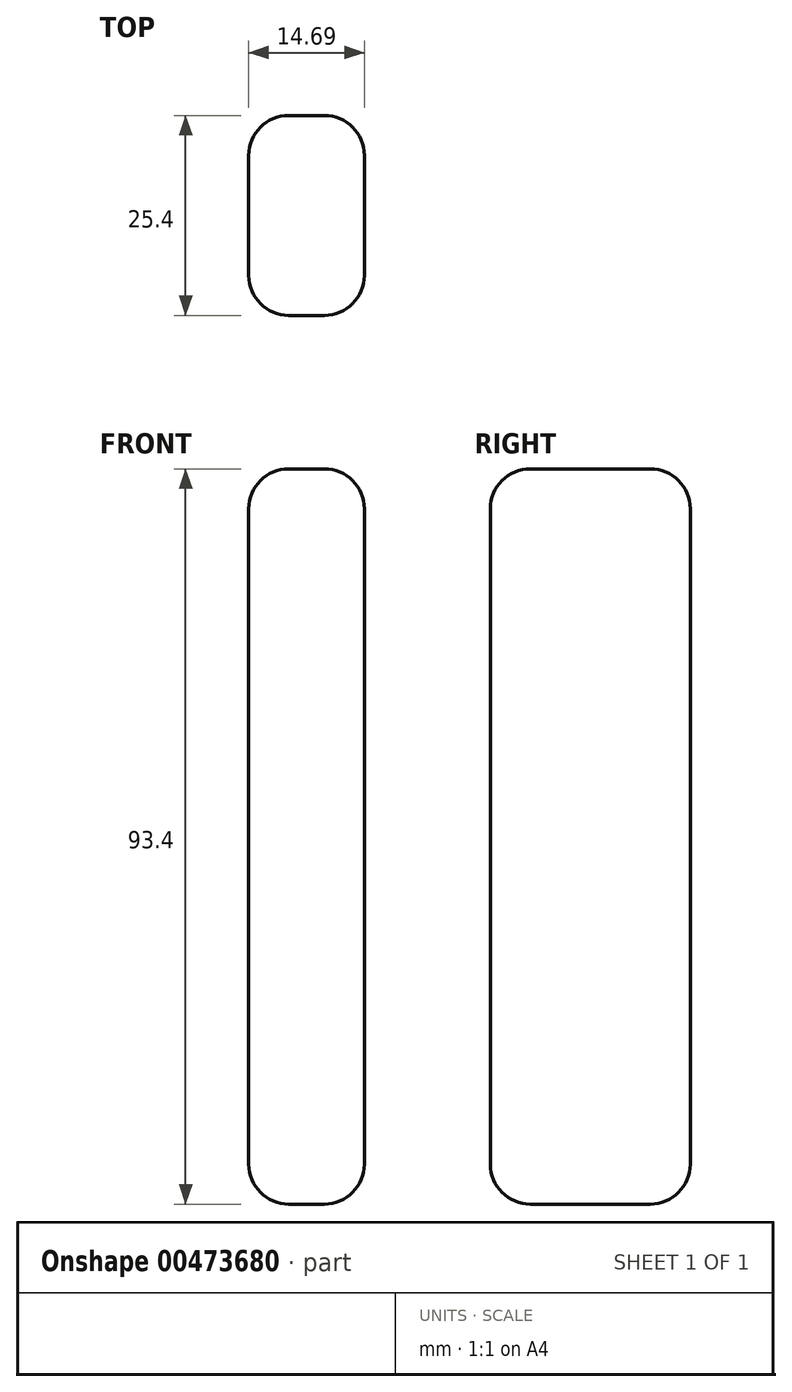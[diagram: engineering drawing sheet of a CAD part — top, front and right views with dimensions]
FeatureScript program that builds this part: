
annotation { "Feature Type Name" : "Feature", "Feature Type Description" : "" }
export const myFeature = defineFeature(function(context is Context, id is Id, definition is map)
    precondition{}
    {
        {
            var Q0;
            Q0=qCreatedBy(makeId("Front.planeOp"),FACE);
            var sketch = newSketch(context, id + "F0", { "sketchPlane" : qUnion([Q0])});
            skLineSegment(sketch, "E0", {"start": v(0, 0) * mm, "end": v(0, -93.4) * mm});
            skLineSegment(sketch, "E1", {"start": v(0, -93.4) * mm, "end": v(14.69, -93.4) * mm});
            skLineSegment(sketch, "E2", {"start": v(14.69, -93.4) * mm, "end": v(14.69, 0) * mm});
            skLineSegment(sketch, "E3", {"start": v(14.69, 0) * mm, "end": v(0, 0) * mm});
            skSolve(sketch);
        }
        {
            var Q0;
            Q0 = qSketchRegion(id + "F0", true);
            extrude(context, id + "F1", {"entities" : qUnion([Q0]), "depth" : 25.4 * mm});
        }
        {
            var Q0;
            Q0=makeQuery(id+"F1.opExtrude","CAP_EDGE",EDGE,{"disambiguationData":[OSD([sQuery(id+"F0.wireOp",EDGE,"E2")])],"isStart":false});
            var Q1;
            Q1=makeQuery(id+"F1.opExtrude","CAP_FACE",FACE,{"disambiguationData":[OSD([sQuery(id+"F0.wireOp",EDGE,"E0"),sQuery(id+"F0.wireOp",EDGE,"E1"),sQuery(id+"F0.wireOp",EDGE,"E2"),sQuery(id+"F0.wireOp",EDGE,"E3")])],"isStart":false});
            fillet(context, id + "F2", {"entities" : qUnion([Q0, Q1]), "radius" : 5.08 * mm, "tangentPropagation" : true, "allowEdgeOverflow" : false});
        }
        {
            var Q0;
            Q0=makeQuery(id+"F1.opExtrude","CAP_EDGE",EDGE,{"disambiguationData":[OSD([sQuery(id+"F0.wireOp",EDGE,"E2")])],"isStart":true});
            var Q1;
            Q1=makeQuery(id+"F1.opExtrude","CAP_EDGE",EDGE,{"disambiguationData":[OSD([sQuery(id+"F0.wireOp",EDGE,"E0")])],"isStart":true});
            fillet(context, id + "F3", {"entities" : qUnion([Q0, Q1]), "radius" : 5.08 * mm, "tangentPropagation" : true, "allowEdgeOverflow" : false});
        }
        {
            var Q0;
            Q0=makeQuery(id+"F1.opExtrude","CAP_EDGE",EDGE,{"disambiguationData":[OSD([sQuery(id+"F0.wireOp",EDGE,"E1")])],"isStart":true});
            var Q1;
            Q1=makeQuery(id+"F1.opExtrude","CAP_EDGE",EDGE,{"disambiguationData":[OSD([sQuery(id+"F0.wireOp",EDGE,"E3")])],"isStart":true});
            fillet(context, id + "F4", {"entities" : qUnion([Q0, Q1]), "radius" : 5.08 * mm, "tangentPropagation" : true, "allowEdgeOverflow" : false});
        }
    });
